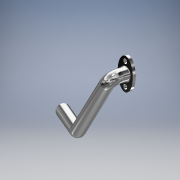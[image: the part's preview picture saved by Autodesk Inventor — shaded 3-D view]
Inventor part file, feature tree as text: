
AUTODESK INVENTOR PART (.ipt)
format: ipt  version: 2018 (Build 220112000, 112)  size: 186,368 bytes
history: native  units: mm
features: sketch x5, plane x2, extrude x1, sweep x1, fillet x1
ambient origin geometry x8: Origin, YZ Plane, XZ Plane, XY Plane, X Axis, Y Axis, Z Axis, Center Point
bodies: Solid1 (feature_tree)
feature tree (10):
  extrude  "Extrusion1"  Depth=6.0mm
  sketch  "Sketch2"  dims[d2=7.0mm d4=3.0mm d5=3.0mm]
  plane  "Work Plane1"
  sketch  "Sketch3"  dims[d6=7.0mm]
  plane  "Work Plane2"
  sweep  "Sweep1"
  fillet  "Fillet1"  Radius=3.0mm
  sketch  "Sketch1"  dims[d0=10.0mm d1=6.0mm]
  sketch  "Sketch4"  dims[d7=7.0mm d8=2.0mm d9=0.0mm d10=2.0mm d11=7.0mm d12=-45.0mm d13=4.487242mm d14=69.478mm d16=15.021mm d17=30.0mm d18=90.0deg d19=8.0mm d20=7.0mm d21=5.0mm d22=5.0mm d23=7.0mm d24=0.0mm d25=0.0mm d26=0.5mm]
  sketch  "3D Sketch1"
